# Revit family: WCPan-WallHung-54cm-Vitra_EqualSeries_7245
name_source: partatom
category: Plumbing Fixtures
revit_build: Autodesk Revit 2017 (Build: 20160225_1515(x64)
units: mm (PartAtom-declared; Revit-internal decimal feet)

## family parameters
Cut with Voids When Loaded = No
Host = Face
OmniClass Number = 23.45.05.21.11
OmniClass Title = Water Closets
Part Type = Normal
Room Calculation Point = No
Round Connector Dimension = Use Diameter
Shared = Yes

## types (6) — shared parameters
BIMobject category = Sanitary - Toilets
Brand = VitrA
Default Elevation = 410 mm
Description = WCPan-WallHung-54cm-Vitra_EqualSeries
Design country = Turkey
HW Connection = No
IFC Classification = Sanitary Terminal
Main Material = Ceramic
Manufacturer = VitrA
Manufacturer name = Vitra
Masterformat 2014 Code = 22 45 26
Masterformat 2014 Description = Sanitary Facilities
Mounting type = Wall Hung
NBS Referans Code = 35-65-90
NBS Referans Description = Toilet Systems
Nominal Depth (mm) = 540 mm  [stored 1.77165 ft]
Nominal Height (mm) = 310 mm
Nominal Width (mm) = 395 mm  [stored 1.29593 ft]
OmniClass Code = 23-31 19 00
OmniClass Description = Toilets
Primary Material = <By Category>
Product certification = https://www.vitraglobal.com
Product family = Equal
Product group = Wall Hung WC
Secondary Material = Stone Grey
UNSPSC Code = 301815
UNSPSC Description = Sanitary Ware
URL = https://www.vitraglobal.com
Uniclass 1.4 Code = L7216
Uniclass 1.4 Description = Toilets
Uniclass 2.0 Code = SS-35-65-90
Uniclass 2.0 Description = Toilet Systems
Uniclass 2015 Code = Pr_40_20_93
Uniclass 2015 Name = Urinal and WC fittings
Uniformat II Code = D2010
Uniformat II Description = Sanitary Facilities
Vent Connection = No
Warranty Period (Year) = 10 Years
Weight Net (kg) = 24.6
Youtube = https://www.youtube.com

## per-type parameters (varying)
| type | Article No. (default) | Color | Model | Product SKU | Product data url | Product url | Technical description | With Bidet Function |
| WC_WallHung_Vitra_EqualSeries_7245B476-0075 | 7245B476-0075 | Stone Grey | 7245B476-0075 | 7245B476-0075 | https://www.vitraglobal.com |  | https://www.vitraglobal.com | No |
| WC_WallHung_Vitra_EqualSeries_7245B476-0090 | 7245B476-0090 | Stone Grey | 7245B476-0090 | 7245B476-0090 | https://www.vitraglobal.com |  | https://www.vitraglobal.com | Yes |
| WC_WallHung_Vitra_EqualSeries_7245B403-0075 | 7245B403-0075 | White | 7245B403-0075 | 7245B403-0075 | https://www.bimobject.com | https://www.vitraglobal.com | https://www.vitraglobal.com | No |
| WC_WallHung_Vitra_EqualSeries_7245B403-0090 | 7245B403-0090 | White | 7245B403-0090 | 7245B403-0090 | https://www.vitraglobal.com |  | https://www.vitraglobal.com | Yes |
| WC_WallHung_Vitra_EqualSeries_7245B403H0075 | 7245B403H0075 | White | 7245B403H0075 | 7245B403H0075 | https://www.bimobject.com | https://www.vitra-india.com | https://www.vitra-india.com | No |
| WC_WallHung_Vitra_EqualSeries_7245B403H0559 | 7245B403H0559 | White | 7245B403H0559 | 7245B403H0559 | https://www.bimobject.com | https://www.vitra-india.com | https://www.vitra-india.com | No |

note: [stored X ft] marks values corroborated as IEEE doubles in the binary element streams (Revit-internal decimal feet)

## geometry (parser evidence)
native form markers: Sweep x2
no freeform markers — native parametric forms only
